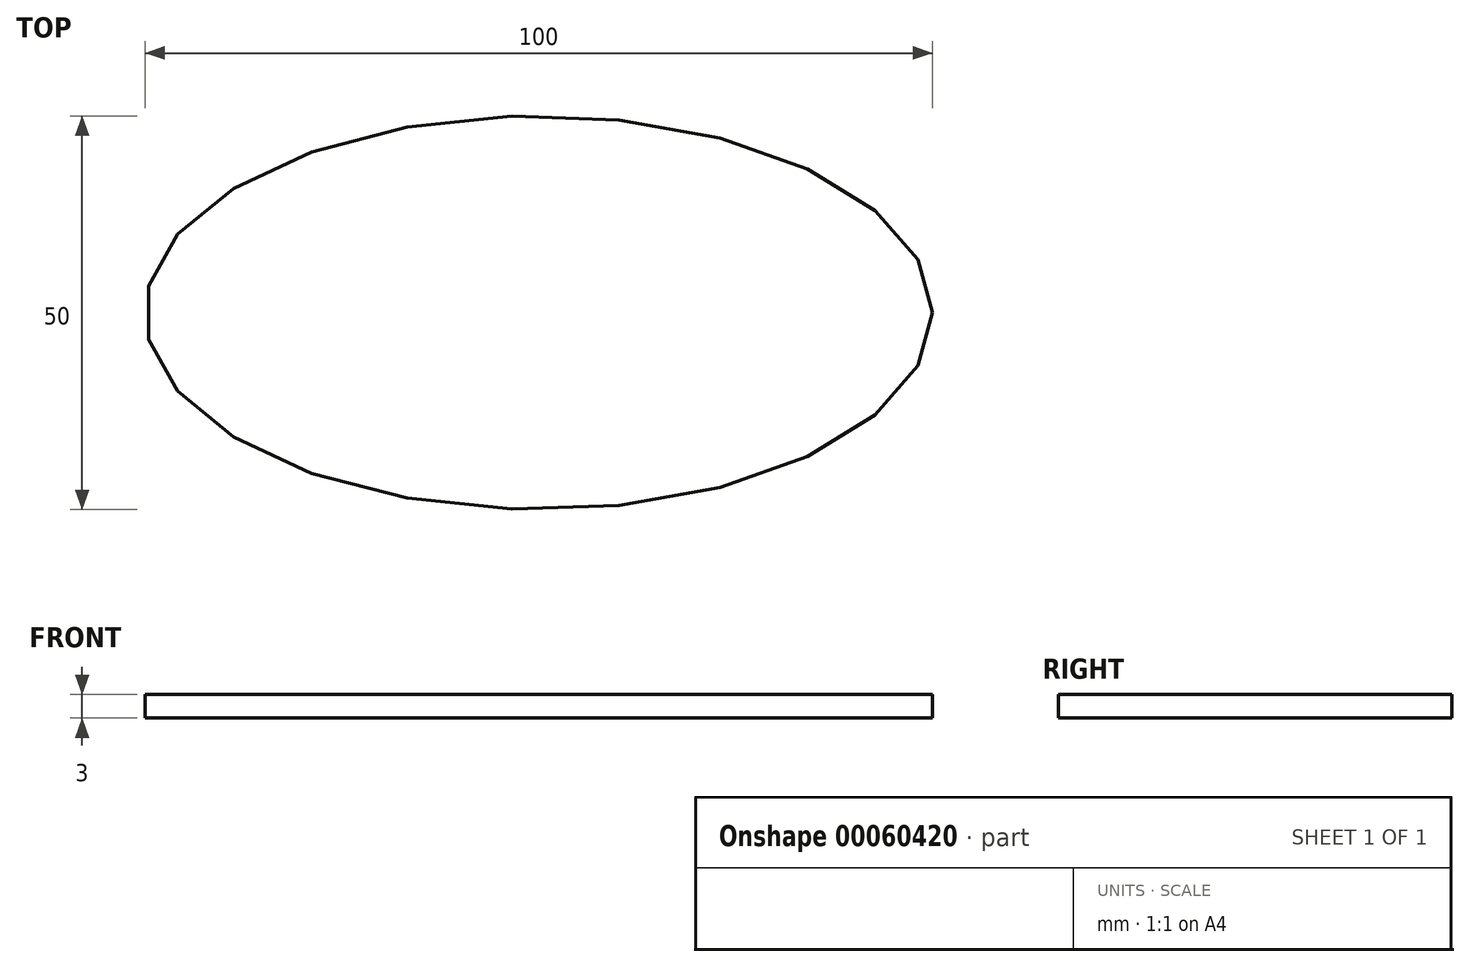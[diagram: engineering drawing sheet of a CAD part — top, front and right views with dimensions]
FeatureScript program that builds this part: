
annotation { "Feature Type Name" : "Feature", "Feature Type Description" : "" }
export const myFeature = defineFeature(function(context is Context, id is Id, definition is map)
    precondition{}
    {
        {
            var Q0;
            Q0=qCreatedBy(makeId("Top.planeOp"),FACE);
            var sketch = newSketch(context, id + "F0", { "sketchPlane" : qUnion([Q0])});
            skEllipse(sketch, "E0", {"center": v(0, 0) * mm, "majorRadius": 50 * mm, "minorRadius": 25 * mm, "majorAxis": v(1, 0)});
            skFitSpline(sketch, "E1.0", {"points": [v(44.9, -1.49) * mm, v(45.05, 0) * mm, v(44.9, 1.49) * mm, v(44.45, 3.03) * mm, v(43.63, 4.66) * mm, v(42.42, 6.37) * mm, v(40.76, 8.12) * mm, v(38.67, 9.88) * mm, v(36.56, 11.3) * mm, v(34.67, 12.4) * mm, v(33.14, 13.21) * mm, v(31.5, 13.98) * mm, v(29.24, 14.96) * mm, v(26.2, 16.09) * mm, v(22.3, 17.26) * mm, v(18.15, 18.23) * mm, v(13.82, 19.01) * mm, v(9.32, 19.58) * mm, v(5.48, 19.86) * mm, v(2.36, 19.98) * mm, v(0, 20) * mm, v(-2.36, 19.98) * mm, v(-5.48, 19.86) * mm, v(-9.32, 19.58) * mm, v(-13.82, 19.01) * mm, v(-18.15, 18.23) * mm, v(-22.3, 17.26) * mm, v(-26.2, 16.09) * mm, v(-29.24, 14.96) * mm, v(-31.5, 13.98) * mm, v(-33.14, 13.21) * mm, v(-34.67, 12.4) * mm, v(-36.56, 11.3) * mm, v(-38.67, 9.88) * mm, v(-40.76, 8.12) * mm, v(-42.42, 6.37) * mm, v(-43.63, 4.66) * mm, v(-44.45, 3.03) * mm, v(-44.9, 1.49) * mm, v(-45.05, 0) * mm, v(-44.9, -1.49) * mm, v(-44.45, -3.03) * mm, v(-43.63, -4.66) * mm, v(-42.42, -6.37) * mm, v(-40.76, -8.12) * mm, v(-38.67, -9.88) * mm, v(-36.56, -11.3) * mm, v(-34.67, -12.4) * mm, v(-33.14, -13.21) * mm, v(-31.5, -13.98) * mm, v(-29.24, -14.96) * mm, v(-26.2, -16.09) * mm, v(-22.3, -17.26) * mm, v(-18.15, -18.23) * mm, v(-13.82, -19.01) * mm, v(-9.32, -19.58) * mm, v(-5.48, -19.86) * mm, v(-2.36, -19.98) * mm, v(0, -20) * mm, v(2.36, -19.98) * mm, v(5.48, -19.86) * mm, v(9.32, -19.58) * mm, v(13.82, -19.01) * mm, v(18.15, -18.23) * mm, v(22.3, -17.26) * mm, v(26.2, -16.09) * mm, v(29.24, -14.96) * mm, v(31.5, -13.98) * mm, v(33.14, -13.21) * mm, v(34.67, -12.4) * mm, v(36.56, -11.3) * mm, v(38.67, -9.88) * mm, v(40.76, -8.12) * mm, v(42.42, -6.37) * mm, v(43.63, -4.66) * mm, v(44.45, -3.03) * mm, v(44.9, -1.49) * mm, v(45.05, 0) * mm, v(44.9, 1.49) * mm, v(44.9, -1.49) * mm]});
            skSolve(sketch);
        }
        {
            var Q0;
            Q0 = qSketchRegion(id + "F0", true);
            extrude(context, id + "F1", {"entities" : qUnion([Q0]), "depth" : 3 * mm});
        }
    });
